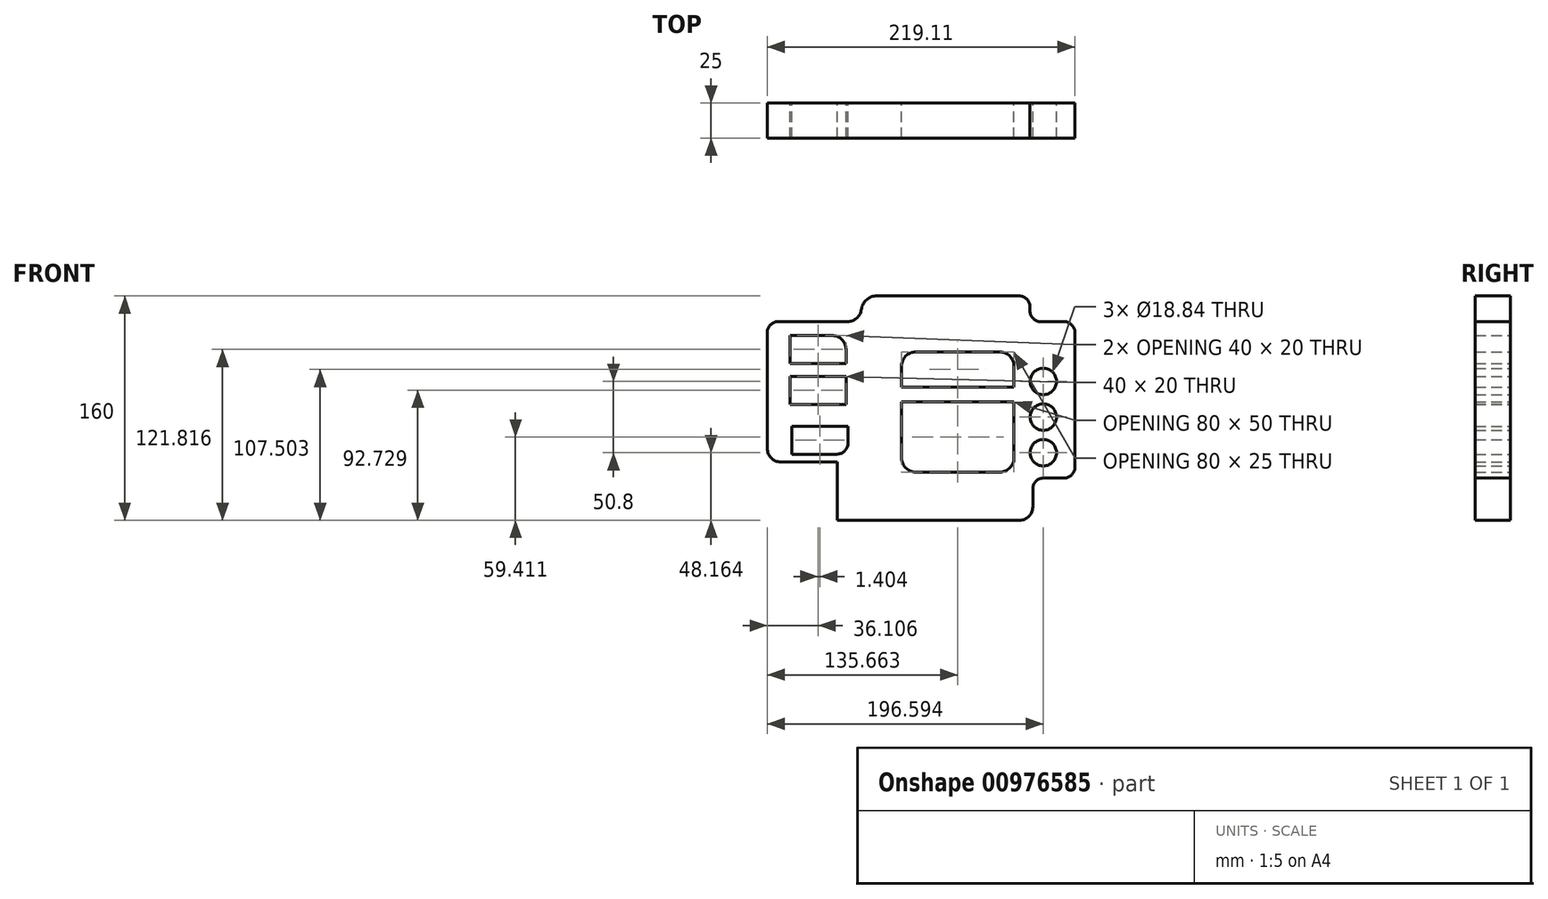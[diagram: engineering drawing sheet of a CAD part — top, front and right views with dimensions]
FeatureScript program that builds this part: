
annotation { "Feature Type Name" : "Feature", "Feature Type Description" : "" }
export const myFeature = defineFeature(function(context is Context, id is Id, definition is map)
    precondition{}
    {
        {
            var Q0;
            Q0=qCreatedBy(makeId("Front.planeOp"),FACE);
            var sketch = newSketch(context, id + "F0", { "sketchPlane" : qUnion([Q0])});
            skLineSegment(sketch, "E0", {"start": v(-119.5, 74.47) * mm, "end": v(-119.5, -25.53) * mm});
            skLineSegment(sketch, "E1", {"start": v(-119.5, 74.47) * mm, "end": v(-62.4, 74.47) * mm});
            skLineSegment(sketch, "E2", {"start": v(-52.4, 84.47) * mm, "end": v(-52.4, 92.85) * mm});
            skLineSegment(sketch, "E3", {"start": v(-52.4, 92.85) * mm, "end": v(67.6, 92.85) * mm});
            skLineSegment(sketch, "E4", {"start": v(67.6, 92.85) * mm, "end": v(67.6, 74.47) * mm});
            skLineSegment(sketch, "E5", {"start": v(67.6, 74.47) * mm, "end": v(99.6, 74.47) * mm});
            skLineSegment(sketch, "E6", {"start": v(99.6, 74.47) * mm, "end": v(99.6, -37) * mm});
            skLineSegment(sketch, "E7", {"start": v(-119.5, -25.53) * mm, "end": v(-69.5, -25.53) * mm});
            skLineSegment(sketch, "E8", {"start": v(-69.5, -25.53) * mm, "end": v(-69.5, -67.15) * mm});
            skLineSegment(sketch, "E9", {"start": v(-69.5, -67.15) * mm, "end": v(69.6, -67.15) * mm});
            skCircle(sketch, "E10", {"center": v(77.1, 31.81) * mm, "radius": 9.42 * mm});
            skCircle(sketch, "E11.0.1.0", {"center": v(77.1, 6.41) * mm, "radius": 9.42 * mm});
            skCircle(sketch, "E11.0.2.0", {"center": v(77.1, -18.99) * mm, "radius": 9.42 * mm});
            skLineSegment(sketch, "E11.direction1", {"start": v(77.1, 31.81) * mm, "end": v(101.35, 31.81) * mm, "construction": true});
            skLineSegment(sketch, "E11.direction2", {"start": v(77.1, 31.81) * mm, "end": v(77.1, 6.41) * mm, "construction": true});
            skLineSegment(sketch, "E12.bottom", {"start": v(-103.4, 64.67) * mm, "end": v(-73.4, 64.67) * mm});
            skLineSegment(sketch, "E12.top", {"start": v(-103.4, 44.67) * mm, "end": v(-63.4, 44.67) * mm});
            skLineSegment(sketch, "E12.left", {"start": v(-103.4, 64.67) * mm, "end": v(-103.4, 44.67) * mm});
            skLineSegment(sketch, "E12.right", {"start": v(-63.4, 54.67) * mm, "end": v(-63.4, 44.67) * mm});
            skLineSegment(sketch, "E13.bottom", {"start": v(-103.4, 35.58) * mm, "end": v(-63.4, 35.58) * mm});
            skLineSegment(sketch, "E13.top", {"start": v(-103.4, 15.58) * mm, "end": v(-63.4, 15.58) * mm});
            skLineSegment(sketch, "E13.left", {"start": v(-103.4, 35.58) * mm, "end": v(-103.4, 15.58) * mm});
            skLineSegment(sketch, "E13.right", {"start": v(-63.4, 35.58) * mm, "end": v(-63.4, 15.58) * mm});
            skLineSegment(sketch, "E14.bottom", {"start": v(-102, 0) * mm, "end": v(-62, 0) * mm});
            skLineSegment(sketch, "E14.top", {"start": v(-102, -20) * mm, "end": v(-62, -20) * mm});
            skLineSegment(sketch, "E14.left", {"start": v(-102, 0) * mm, "end": v(-102, -20) * mm});
            skLineSegment(sketch, "E14.right", {"start": v(-62, 0) * mm, "end": v(-62, -20) * mm});
            skLineSegment(sketch, "E15.bottom", {"start": v(-23.84, 17.26) * mm, "end": v(56.16, 17.26) * mm});
            skLineSegment(sketch, "E16.bottom", {"start": v(-23.84, 27.85) * mm, "end": v(56.16, 27.85) * mm});
            skLineSegment(sketch, "E16.top", {"start": v(-13.84, 52.85) * mm, "end": v(46.16, 52.85) * mm});
            skLineSegment(sketch, "E16.left", {"start": v(-23.84, 27.85) * mm, "end": v(-23.84, 42.85) * mm});
            skLineSegment(sketch, "E16.right", {"start": v(56.16, 27.85) * mm, "end": v(56.16, 42.85) * mm});
            skPoint(sketch, "E17.visualSharp", {"position": v(-52.4, 92.85) * mm});
            skLineSegment(sketch, "E17.filletArc", {"start": v(-52.4, 92.85) * mm, "end": v(-52.4, 92.85) * mm});
            skPoint(sketch, "E18.visualSharp", {"position": v(-63.4, 64.67) * mm});
            skArc(sketch, "E18.filletArc", {"start": v(-63.4, 54.67) * mm, "mid": v(-66.32, 61.74) * mm, "end": v(-73.4, 64.67) * mm});
            skPoint(sketch, "E19.visualSharp", {"position": v(-23.84, 52.85) * mm});
            skArc(sketch, "E19.filletArc", {"start": v(-13.84, 52.85) * mm, "mid": v(-20.9, 49.92) * mm, "end": v(-23.84, 42.85) * mm});
            skPoint(sketch, "E20.visualSharp", {"position": v(56.16, 52.85) * mm});
            skArc(sketch, "E20.filletArc", {"start": v(56.16, 42.85) * mm, "mid": v(53.23, 49.92) * mm, "end": v(46.16, 52.85) * mm});
            skLineSegment(sketch, "E21", {"start": v(-23.84, 17.26) * mm, "end": v(-23.84, -22.74) * mm});
            skLineSegment(sketch, "E22", {"start": v(56.16, 17.26) * mm, "end": v(56.16, -22.74) * mm});
            skLineSegment(sketch, "E23", {"start": v(-13.84, -32.74) * mm, "end": v(46.16, -32.74) * mm});
            skPoint(sketch, "E24.visualSharp", {"position": v(-23.84, -32.74) * mm});
            skArc(sketch, "E24.filletArc", {"start": v(-23.84, -22.74) * mm, "mid": v(-20.9, -29.81) * mm, "end": v(-13.84, -32.74) * mm});
            skPoint(sketch, "E25.visualSharp", {"position": v(56.16, -32.74) * mm});
            skArc(sketch, "E25.filletArc", {"start": v(46.16, -32.74) * mm, "mid": v(53.23, -29.81) * mm, "end": v(56.16, -22.74) * mm});
            skLineSegment(sketch, "E26", {"start": v(69.6, -67.15) * mm, "end": v(69.6, -37) * mm});
            skLineSegment(sketch, "E27", {"start": v(69.6, -37) * mm, "end": v(99.6, -37) * mm});
            skPoint(sketch, "E28.visualSharp", {"position": v(-52.4, 74.47) * mm});
            skArc(sketch, "E28.filletArc", {"start": v(-62.4, 74.47) * mm, "mid": v(-55.32, 77.4) * mm, "end": v(-52.4, 84.47) * mm});
            skSolve(sketch);
        }
        {
            var Q0;
            Q0=makeQuery(id+"F0.imprint","IMPRINT",FACE,{"disambiguationData":[TD([[makeQuery(id+"F0.imprint","IMPRINT",EDGE,{"derivedFrom":sQuery(id+"F0.wireOp",EDGE,"E0")}),1.0]])]});
            extrude(context, id + "F1", {"entities" : qUnion([Q0]), "depth" : 25 * mm, "offsetDistance" : 25 * mm});
        }
        {
            var Q0;
            Q0=makeQuery(id+"F1.opExtrude","SWEPT_EDGE",EDGE,{"disambiguationData":[OSD([sQuery(id+"F0.wireOp",EDGE,"E2"),sQuery(id+"F0.wireOp",EDGE,"E3")])]});
            fillet(context, id + "F2", {"entities" : qUnion([Q0]), "radius" : 11.1 * mm, "tangentPropagation" : true, "allowEdgeOverflow" : false});
        }
        {
            var Q0;
            Q0=makeQuery(id+"F1.opExtrude","SWEPT_EDGE",EDGE,{"disambiguationData":[OSD([sQuery(id+"F0.wireOp",EDGE,"E0"),sQuery(id+"F0.wireOp",EDGE,"E7")])]});
            var Q1;
            Q1=makeQuery(id+"F1.opExtrude","SWEPT_EDGE",EDGE,{"disambiguationData":[OSD([sQuery(id+"F0.wireOp",EDGE,"E9"),sQuery(id+"F0.wireOp",EDGE,"E26")])]});
            fillet(context, id + "F3", {"entities" : qUnion([Q0, Q1]), "radius" : 9.42 * mm, "tangentPropagation" : true, "allowEdgeOverflow" : false});
        }
        {
            var Q0;
            Q0=makeQuery(id+"F1.opExtrude","SWEPT_EDGE",EDGE,{"disambiguationData":[OSD([sQuery(id+"F0.wireOp",EDGE,"E3"),sQuery(id+"F0.wireOp",EDGE,"E4")])]});
            var Q1;
            Q1=makeQuery(id+"F1.opExtrude","SWEPT_EDGE",EDGE,{"disambiguationData":[OSD([sQuery(id+"F0.wireOp",EDGE,"E4"),sQuery(id+"F0.wireOp",EDGE,"E5")])]});
            var Q2;
            Q2=makeQuery(id+"F1.opExtrude","SWEPT_EDGE",EDGE,{"disambiguationData":[OSD([sQuery(id+"F0.wireOp",EDGE,"E5"),sQuery(id+"F0.wireOp",EDGE,"E6")])]});
            var Q3;
            Q3=makeQuery(id+"F1.opExtrude","SWEPT_EDGE",EDGE,{"disambiguationData":[OSD([sQuery(id+"F0.wireOp",EDGE,"E0"),sQuery(id+"F0.wireOp",EDGE,"E1")])]});
            var Q4;
            Q4=makeQuery(id+"F1.opExtrude","SWEPT_EDGE",EDGE,{"disambiguationData":[OSD([sQuery(id+"F0.wireOp",EDGE,"E6"),sQuery(id+"F0.wireOp",EDGE,"E27")])]});
            var Q5;
            Q5=makeQuery(id+"F1.opExtrude","SWEPT_EDGE",EDGE,{"disambiguationData":[OSD([sQuery(id+"F0.wireOp",EDGE,"E26"),sQuery(id+"F0.wireOp",EDGE,"E27")])]});
            fillet(context, id + "F4", {"entities" : qUnion([Q0, Q1, Q2, Q3, Q4, Q5]), "radius" : 7.73 * mm, "tangentPropagation" : true, "allowEdgeOverflow" : false});
        }
        {
            var Q0;
            Q0=makeQuery(id+"F1.opExtrude","SWEPT_EDGE",EDGE,{"disambiguationData":[OSD([sQuery(id+"F0.wireOp",EDGE,"E14.top"),sQuery(id+"F0.wireOp",EDGE,"E14.right")])]});
            fillet(context, id + "F5", {"entities" : qUnion([Q0]), "radius" : 7.97 * mm, "tangentPropagation" : true, "allowEdgeOverflow" : false});
        }
    });
